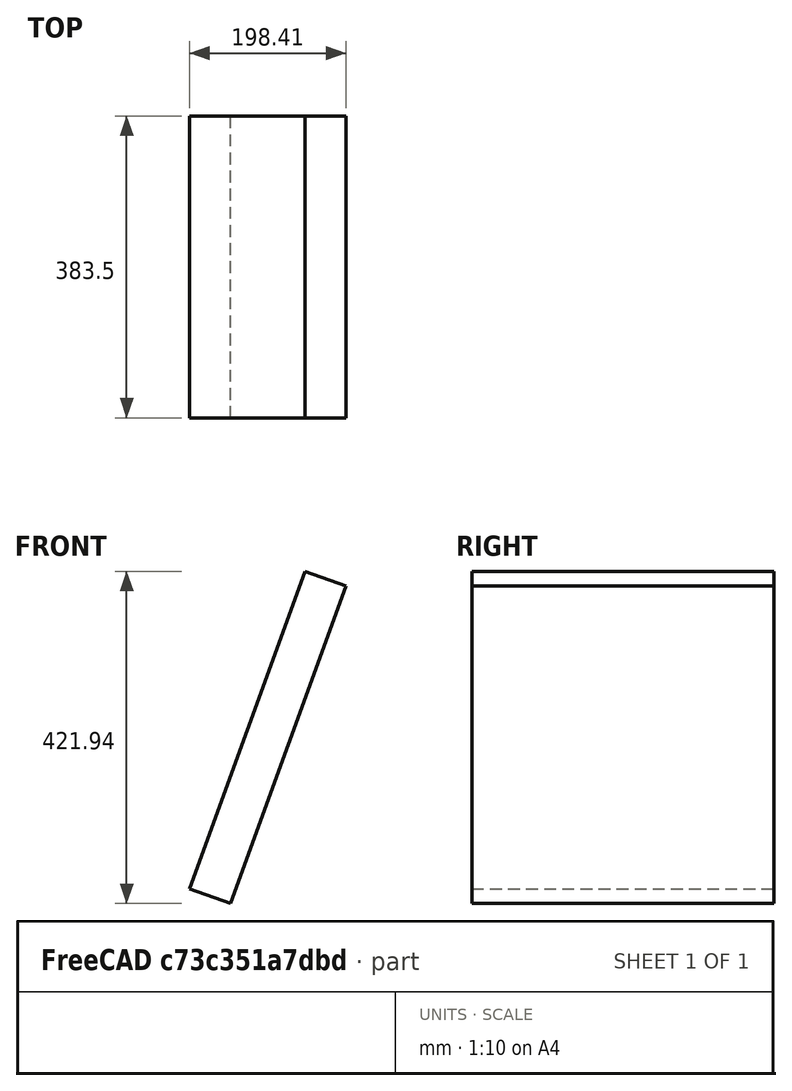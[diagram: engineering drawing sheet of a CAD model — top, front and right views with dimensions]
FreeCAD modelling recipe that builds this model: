
FCSTD DOCUMENT  (FreeCAD 0.19R24276 (Git))
Label: 1106_Monitor_AL1913
License: All rights reserved
LicenseURL: http://en.wikipedia.org/wiki/All_rights_reserved
objects: Spreadsheet::Sheet×1, Sketcher::SketchObject×1, PartDesign::Pad×1, PartDesign::Body×1, App::Part×1
note: 4 computed .brp shape members not serialized (recipe doc carries the construction recipe); baked Part::Feature solids carry a one-line shape summary decoded from their .brp

FEATURE [Spreadsheet::Sheet] Spreadsheet  label="XLS"
  cells = B3=Monitor dimensions; G3=Panel Type; J3=Speakers; B4=Width; C4(W_monitor)=427; D4=W_monitor; G4=Size; H4=19 inch monitor; J4=DVI; K4=DVI-D connector; B5=Height; C5(H_monitor)=429; D5=H_monitor; G5=Screen Resolution; H5=1280 x 1024; J5=VGA; B6=Depth; C6(D_monitor)=55; D6=D_monitor; G6=Hertz; H6=75Hz refresh rate; J6=HDMI; G7=Weight; H7==4.5kg; J7=Displayport; B8=Monitor Mounting; G8=Width; H8==427mm; J8=SCART; B9=Width; C9(W_mount)=75; D9=W_mount; G9=Height; H9==429mm; J9=D - Sub; K9=x; B10=Height; C10(H_mount)=75; D10=H_mount; G10=Depth; H10==196mm; J10=Audio InOut; K10=x; B11=HeightMounting; C11(H0_mount)=100; D11=H0_mount; G11=Response; H11=If you know the response time of the monitor in question then please let us know and we will update this area; J11=Energy Save; K11=x; B12=ScrewSize; C12(D_screw)=8; D12=D_screw; G12=Brightness; H12=300cd/m²; J12=Tilt Stand; K12=x; G13=Contrast; H13=800:1; J13=Wall Mount; G14=Viewing Angles; H14=170° hor / 170° ver; J14=Optical Out; G15=Power; H15=65Watts; J15=Component; G16=Colors; H16=16.2 million; J16=Headphone; G17=USB Hub; H17=No USB hub; J17=CI Slot
FEATURE [Sketcher::SketchObject] Sketch002
  FullyConstrained = true
  MapMode = 5
  Placement = pos=(0,0,0) rot=(0,0.707107,0.707107;3.14159rad)
  Support = -> [XZ_Plane001]
  expr: Constraints[7] = <<XLS>>.D_monitor
  expr: Constraints[8] = <<XLS>>.H_monitor
  sketch-geometry (7):
    g0: LineSegment StartX=40 StartY=50 StartZ=0 EndX=-106.727 EndY=453.128 EndZ=0
    g1: LineSegment StartX=-106.727 StartY=453.128 StartZ=0 EndX=-55.0435 EndY=471.939 EndZ=0
    g2: LineSegment StartX=-55.0435 StartY=471.939 StartZ=0 EndX=91.6831 EndY=68.8111 EndZ=0
    g3: LineSegment StartX=91.6831 StartY=68.8111 StartZ=0 EndX=40 EndY=50 EndZ=0
    g4: LineSegment StartX=40 StartY=50 StartZ=0 EndX=0 EndY=0 EndZ=0
    g5: LineSegment StartX=0 StartY=0 StartZ=0 EndX=0 EndY=50 EndZ=0
    g6: LineSegment StartX=0 StartY=50 StartZ=0 EndX=40 EndY=50 EndZ=0
  constraints (19):
    c: Coincident(g2,g1)
    c: Coincident(g3,g2)
    c: Coincident(g3,g0)
    c: Perpendicular(g1,g0)
    c: Perpendicular(g2,g1)
    c: Perpendicular(g2,g3)
    c: Coincident(g1,g0)
    c: Distance(g1) = 55
    c: Distance(g2) = 429
    c: Coincident(g4,g0)
    c: Coincident(g4,g-1)
    c: Coincident(g5,g-1)
    c: PointOnObject(g5,g-2)
    c: Coincident(g6,g5)
    c: Coincident(g6,g0)
    c: Horizontal(g6)
    c: Distance(g5) = 50
    c: Distance(g6) = 40
    c: Angle(g0,g6) = 1.22173
FEATURE [PartDesign::Pad] Pad002
  AllowMultiFace = false
  Direction = (1,1,1)
  Length = 213.5
  Length2 = 170
  Placement = pos=(0,0,0) rot=(1,0,0;1.5708rad)
  Profile = -> Sketch002
  Type = 4
  expr: Length = <<XLS>>.W_monitor / 2
FEATURE [PartDesign::Body] Pad002Body
  Group = -> [Sketch002,Pad002]
  Origin = -> Origin001
  Tip = -> Pad002
FEATURE [App::Part] Part
  Group = -> [Pad002Body]
  License = CC BY 3.0
  LicenseURL = http://creativecommons.org/licenses/by/3.0/
  Origin = -> Origin
